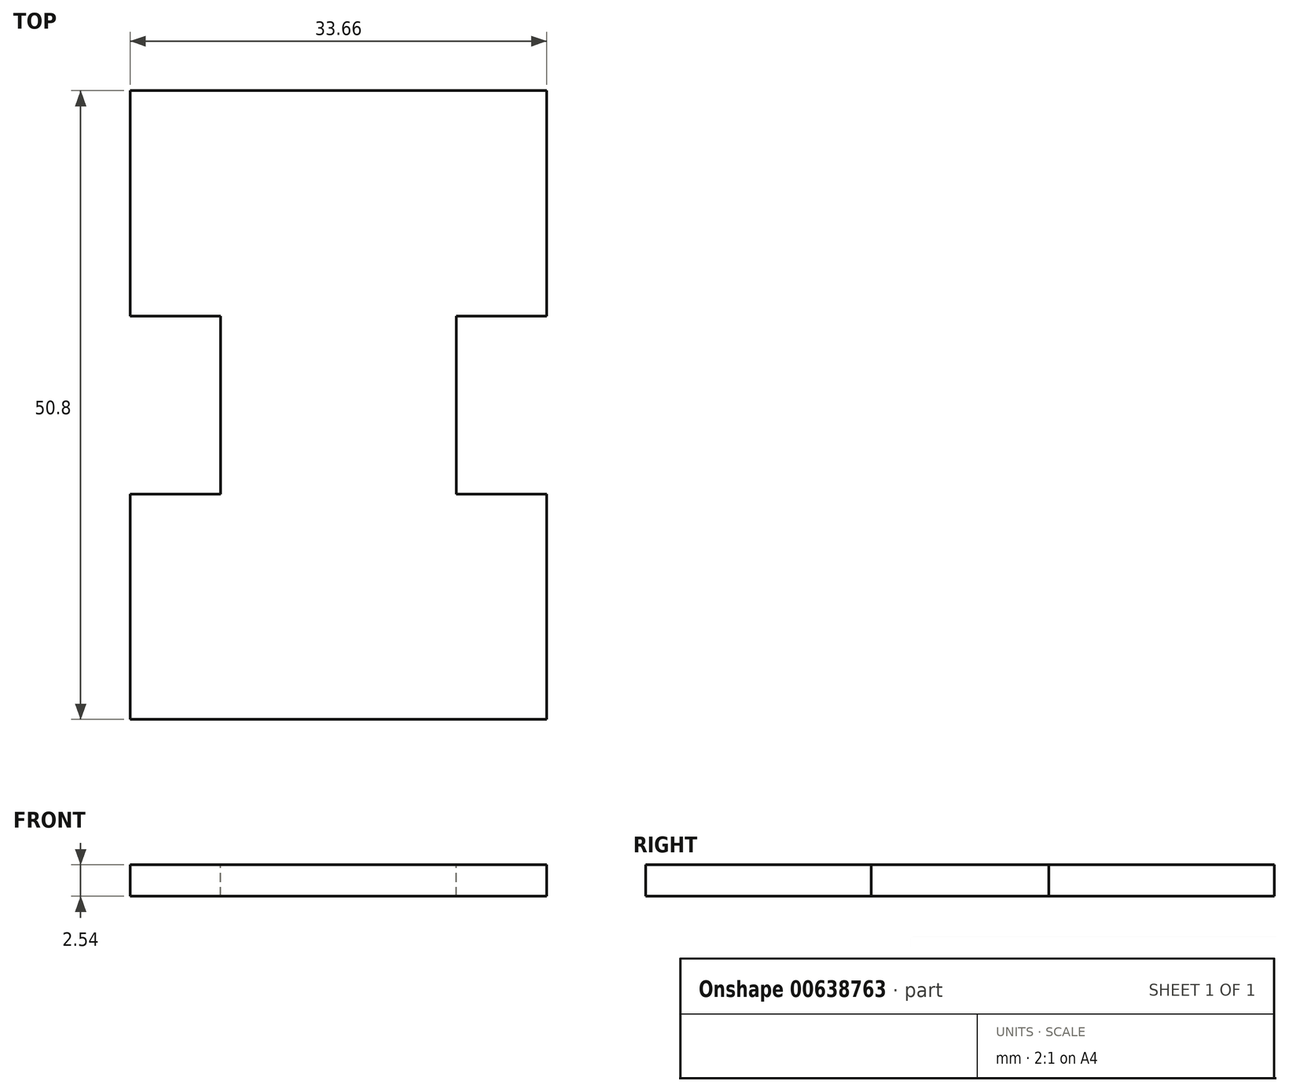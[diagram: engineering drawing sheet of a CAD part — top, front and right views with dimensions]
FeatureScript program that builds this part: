
annotation { "Feature Type Name" : "Feature", "Feature Type Description" : "" }
export const myFeature = defineFeature(function(context is Context, id is Id, definition is map)
    precondition{}
    {
        {
            var Q0;
            Q0=qCreatedBy(makeId("Top.planeOp"),FACE);
            var sketch = newSketch(context, id + "F0", { "sketchPlane" : qUnion([Q0])});
            skLineSegment(sketch, "E0", {"start": v(-16.83, -36.82) * mm, "end": v(16.83, -36.82) * mm});
            skLineSegment(sketch, "E1", {"start": v(-18.73, 15.87) * mm, "end": v(-16.83, 35.99) * mm});
            skLineSegment(sketch, "E2", {"start": v(-16.83, 35.99) * mm, "end": v(16.83, 35.99) * mm});
            skLineSegment(sketch, "E3", {"start": v(16.83, 35.99) * mm, "end": v(19.12, 15.87) * mm});
            skLineSegment(sketch, "E4", {"start": v(-18.73, 15.87) * mm, "end": v(19.12, 15.87) * mm});
            skLineSegment(sketch, "E5", {"start": v(-16.83, -55.03) * mm, "end": v(16.83, -55.03) * mm});
            skLineSegment(sketch, "E6", {"start": v(-9.53, -29.63) * mm, "end": v(9.53, -29.63) * mm});
            skLineSegment(sketch, "E7", {"start": v(-9.53, -29.63) * mm, "end": v(-9.53, -36.82) * mm});
            skLineSegment(sketch, "E8", {"start": v(9.53, -29.63) * mm, "end": v(9.53, -36.82) * mm});
            skLineSegment(sketch, "E9", {"start": v(-16.83, -36.82) * mm, "end": v(-16.83, -55.03) * mm});
            skLineSegment(sketch, "E10", {"start": v(16.83, -36.82) * mm, "end": v(16.83, -55.03) * mm});
            skLineSegment(sketch, "E11.MirrorCS", {"start": v(9.53, -29.63) * mm, "end": v(9.53, -22.45) * mm});
            skLineSegment(sketch, "E12.MirrorCS", {"start": v(16.83, -22.45) * mm, "end": v(16.83, -4.23) * mm});
            skLineSegment(sketch, "E13.MirrorCS", {"start": v(-16.83, -4.23) * mm, "end": v(16.83, -4.23) * mm});
            skLineSegment(sketch, "E14.MirrorCS", {"start": v(-16.83, -22.45) * mm, "end": v(-16.83, -4.23) * mm});
            skLineSegment(sketch, "E15.MirrorCS", {"start": v(-16.83, -22.45) * mm, "end": v(16.83, -22.45) * mm});
            skLineSegment(sketch, "E16.MirrorCS", {"start": v(-9.53, -29.63) * mm, "end": v(-9.53, -22.45) * mm});
            skSolve(sketch);
        }
        {
            var Q0;
            {var subQ3=sQuery(id+"F0.wireOp",EDGE,"E12.MirrorCS");Q0=makeQuery(id+"F0.imprint","IMPRINT",FACE,{"disambiguationData":[TD([[makeQuery(id+"F0.imprint","IMPRINT",EDGE,{"derivedFrom":subQ3}),1.0]])]});}
            var Q1;
            Q1=makeQuery(id+"F0.imprint","IMPRINT",FACE,{"disambiguationData":[TD([[makeQuery(id+"F0.imprint","IMPRINT",EDGE,{"derivedFrom":sQuery(id+"F0.wireOp",EDGE,"E6")}),1.0]])]});
            var Q2;
            Q2=makeQuery(id+"F0.imprint","IMPRINT",FACE,{"disambiguationData":[TD([[makeQuery(id+"F0.imprint","IMPRINT",EDGE,{"derivedFrom":sQuery(id+"F0.wireOp",EDGE,"E6")}),-1.0]])]});
            var Q3;
            Q3=makeQuery(id+"F0.imprint","IMPRINT",FACE,{"disambiguationData":[TD([[makeQuery(id+"F0.imprint","IMPRINT",EDGE,{"derivedFrom":sQuery(id+"F0.wireOp",EDGE,"E5")}),1.0]])]});
            extrude(context, id + "F1", {"entities" : qUnion([Q0, Q1, Q2, Q3]), "oppositeDirection" : true, "depth" : 2.54 * mm, "offsetDistance" : 25.4 * mm});
        }
    });
